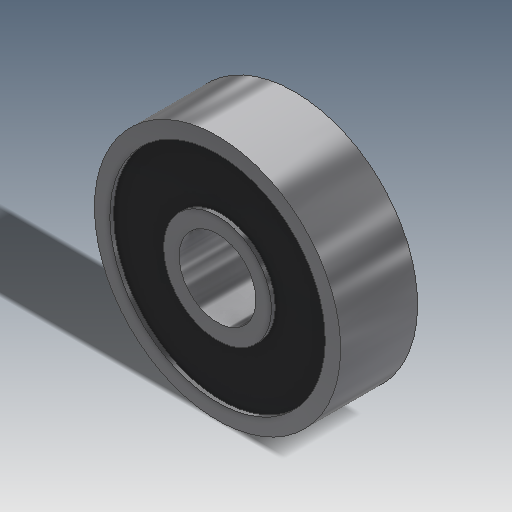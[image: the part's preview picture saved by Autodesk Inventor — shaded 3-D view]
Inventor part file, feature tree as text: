
AUTODESK INVENTOR PART (.ipt)
format: ipt  version: 2020 (Build 240168000, 168)  size: 165,376 bytes
history: native  units: in
note: dims shown in document units (in); Inventor stores cm internally (conversion verified against a paired STEP export)
features: revolve x1, sketch x1
ambient origin geometry x8: Origin, YZ Plane, XZ Plane, XY Plane, X Axis, Y Axis, Z Axis, Center Point
bodies: Solid1 (feature_tree)
feature tree (2):
  revolve  "Revolution1"  [1 undecoded]
  sketch  "Sketch1"  dims[d0=0.1969in d1=0.6299in d2=0.0394in d3=0.0394in d4=0.0098in d5=0.0098in d6=0.1969in d7=90.0deg]
note: 1 required parameter value undecoded (feature->parameter linkage not recoverable at this tier; creation-order binding heuristic only, values carry confidence <= 0.55)
